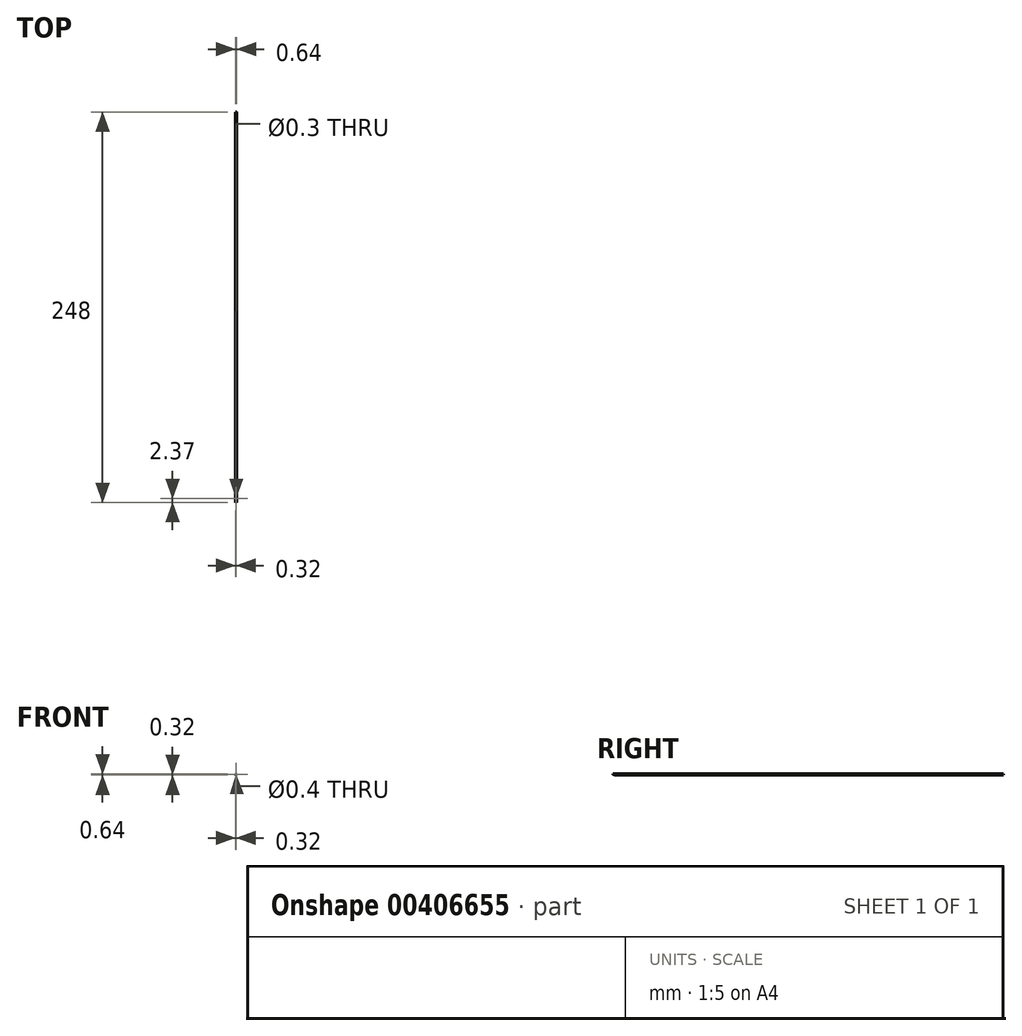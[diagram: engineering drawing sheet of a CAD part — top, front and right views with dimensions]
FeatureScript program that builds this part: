
annotation { "Feature Type Name" : "Feature", "Feature Type Description" : "" }
export const myFeature = defineFeature(function(context is Context, id is Id, definition is map)
    precondition{}
    {
        {
            var Q0;
            Q0=qCreatedBy(makeId("Front.planeOp"),FACE);
            var sketch = newSketch(context, id + "F0", { "sketchPlane" : qUnion([Q0])});
            skCircle(sketch, "E0", {"center": v(0, 0) * mm, "radius": 0.32 * mm});
            skCircle(sketch, "E1.0", {"center": v(0, 0) * mm, "radius": 0.2 * mm});
            skLineSegment(sketch, "E2", {"start": v(-0.34, 0.32) * mm, "end": v(0.4, 0.32) * mm});
            skSolve(sketch);
        }
        {
            var Q0;
            Q0=qSketchRegion(id+"F0",true);
            extrude(context, id + "F1", {"entities" : qUnion([Q0]), "oppositeDirection" : true, "depth" : 248 * mm});
        }
        {
            var Q0;
            Q0=sQuery(id+"F0.wireOp",EDGE,"E2");
            var Q1;
            Q1=makeQuery(id+"F1.opExtrude","SWEPT_FACE",FACE,{"disambiguationData":[OSD([sQuery(id+"F0.wireOp",EDGE,"E0")])]});
            cPlane(context, id + "F2", {"entities" : qUnion([Q0, Q1]), "cplaneType" : CPlaneType.LINE_ANGLE, "offset" : 25 * mm, "angle" : 25 * degree, "oppositeDirection" : true, "width" : 150 * mm, "height" : 150 * mm});
        }
        {
            var Q0;
            Q0=qCreatedBy(id+"F2.planeOp",FACE);
            var sketch = newSketch(context, id + "F3", { "sketchPlane" : qUnion([Q0])});
            skLineSegment(sketch, "E3.bottom", {"start": v(-1.32, -2.2) * mm, "end": v(1.28, -2.2) * mm});
            skLineSegment(sketch, "E3.top", {"start": v(-1.32, 1.1) * mm, "end": v(1.28, 1.1) * mm});
            skLineSegment(sketch, "E3.left", {"start": v(-1.32, -2.2) * mm, "end": v(-1.32, 1.1) * mm});
            skLineSegment(sketch, "E3.right", {"start": v(1.28, -2.2) * mm, "end": v(1.28, 1.1) * mm});
            skSolve(sketch);
        }
        {
            var Q0;
            Q0 = qSketchRegion(id + "F3", true);
            extrude(context, id + "F4", {"entities" : qUnion([Q0]), "operationType" : NewBodyOperationType.REMOVE, "depth" : 25 * mm});
        }
        {
            var Q0;
            Q0=qCreatedBy(makeId("Top.planeOp"),FACE);
            var sketch = newSketch(context, id + "F5", { "sketchPlane" : qUnion([Q0])});
            skCircle(sketch, "E4", {"center": v(0, 2.37) * mm, "radius": 0.15 * mm});
            skSolve(sketch);
        }
        {
            var Q0;
            Q0 = qSketchRegion(id + "F5", true);
            extrude(context, id + "F6", {"entities" : qUnion([Q0]), "operationType" : NewBodyOperationType.REMOVE, "depth" : 25 * mm});
        }
    });
